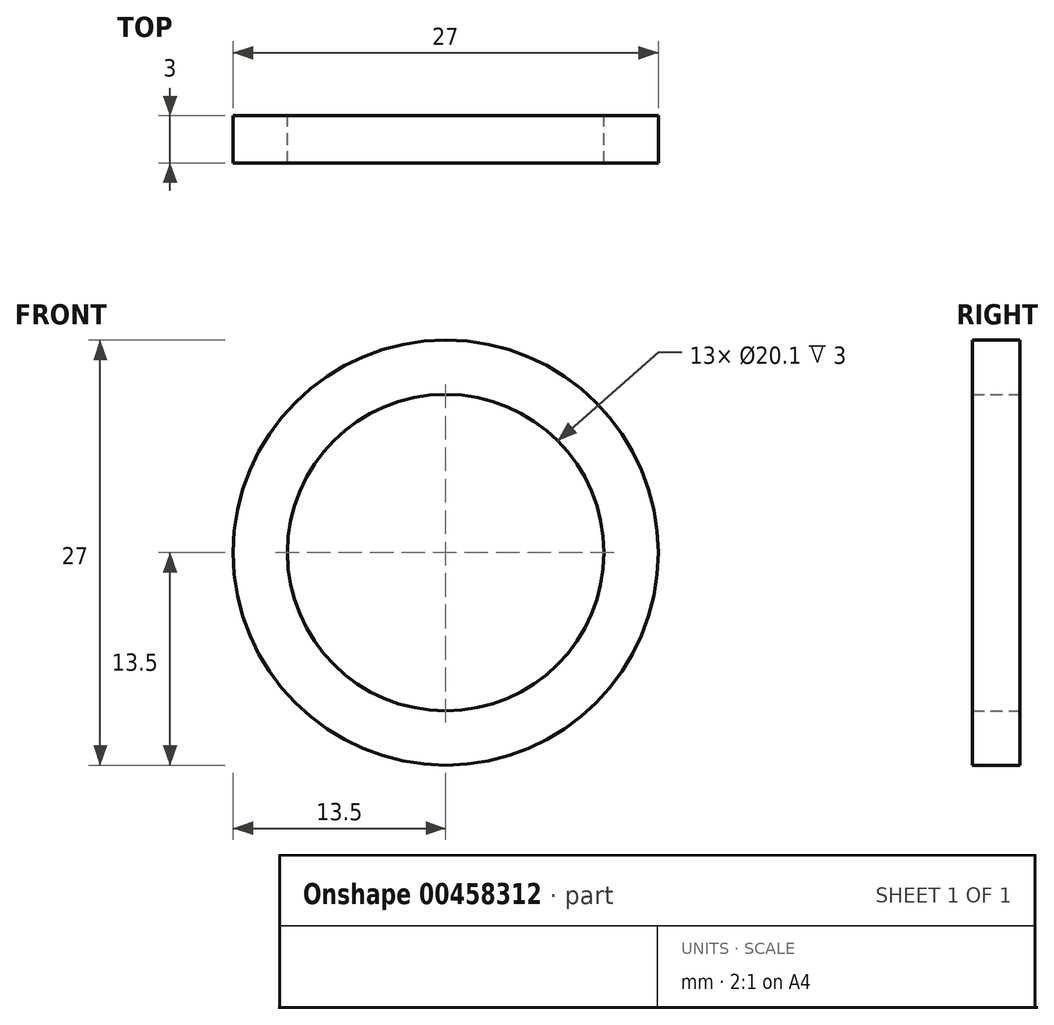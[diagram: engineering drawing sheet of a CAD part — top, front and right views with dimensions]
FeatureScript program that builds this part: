
annotation { "Feature Type Name" : "Feature", "Feature Type Description" : "" }
export const myFeature = defineFeature(function(context is Context, id is Id, definition is map)
    precondition{}
    {
        {
            var Q0;
            Q0=qCreatedBy(makeId("Front.planeOp"),FACE);
            var sketch = newSketch(context, id + "F0", { "sketchPlane" : qUnion([Q0])});
            skCircle(sketch, "E0", {"center": v(0, 0) * mm, "radius": 10.05 * mm});
            skCircle(sketch, "E1", {"center": v(0, 0) * mm, "radius": 13.5 * mm});
            skSolve(sketch);
        }
        {
            var Q0;
            Q0 = qSketchRegion(id + "F0", true);
            var Q1;
            Q1=makeQuery(id+"F0.imprint","IMPRINT",FACE,{"disambiguationData":[TD([[makeQuery(id+"F0.imprint","IMPRINT",EDGE,{"derivedFrom":sQuery(id+"F0.wireOp",EDGE,"E0")}),-1.0]])]});
            extrude(context, id + "F1", {"entities" : qUnion([Q0, Q1]), "depth" : 3 * mm});
        }
    });
